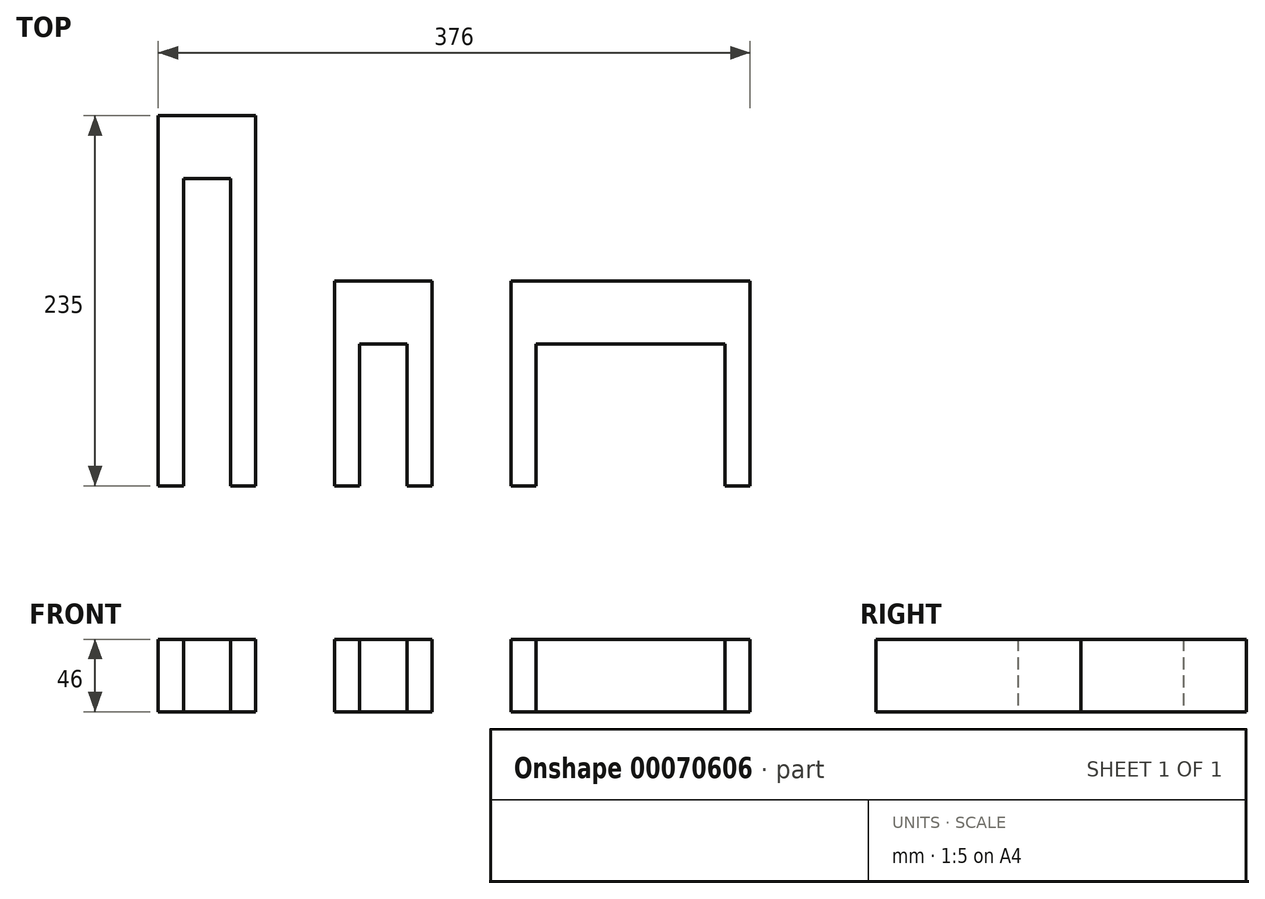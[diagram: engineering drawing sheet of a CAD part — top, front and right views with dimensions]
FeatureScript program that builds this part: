
annotation { "Feature Type Name" : "Feature", "Feature Type Description" : "" }
export const myFeature = defineFeature(function(context is Context, id is Id, definition is map)
    precondition{}
    {
        {
            var Q0;
            Q0=qCreatedBy(makeId("Top.planeOp"),FACE);
            var sketch = newSketch(context, id + "F0", { "sketchPlane" : qUnion([Q0])});
            skLineSegment(sketch, "E0.bottom", {"start": v(-62, 235) * mm, "end": v(0, 235) * mm});
            skLineSegment(sketch, "E0.top", {"start": v(-62, 0) * mm, "end": v(0, 0) * mm});
            skLineSegment(sketch, "E0.left", {"start": v(-62, 235) * mm, "end": v(-62, 0) * mm});
            skLineSegment(sketch, "E0.right", {"start": v(0, 235) * mm, "end": v(0, 0) * mm});
            skLineSegment(sketch, "E1.bottom", {"start": v(50, 130) * mm, "end": v(112, 130) * mm});
            skLineSegment(sketch, "E1.top", {"start": v(50, 0) * mm, "end": v(112, 0) * mm});
            skLineSegment(sketch, "E1.left", {"start": v(50, 130) * mm, "end": v(50, 0) * mm});
            skLineSegment(sketch, "E1.right", {"start": v(112, 130) * mm, "end": v(112, 0) * mm});
            skLineSegment(sketch, "E2.bottom", {"start": v(162, 0) * mm, "end": v(314, 0) * mm});
            skLineSegment(sketch, "E2.top", {"start": v(162, 130) * mm, "end": v(314, 130) * mm});
            skLineSegment(sketch, "E2.left", {"start": v(162, 0) * mm, "end": v(162, 130) * mm});
            skLineSegment(sketch, "E2.right", {"start": v(314, 0) * mm, "end": v(314, 130) * mm});
            skLineSegment(sketch, "E3.bottom", {"start": v(-46, 0) * mm, "end": v(-16, 0) * mm});
            skLineSegment(sketch, "E3.top", {"start": v(-46, 195) * mm, "end": v(-16, 195) * mm});
            skLineSegment(sketch, "E3.left", {"start": v(-46, 0) * mm, "end": v(-46, 195) * mm});
            skLineSegment(sketch, "E3.right", {"start": v(-16, 0) * mm, "end": v(-16, 195) * mm});
            skLineSegment(sketch, "E4.bottom", {"start": v(66, 0) * mm, "end": v(96, 0) * mm});
            skLineSegment(sketch, "E4.top", {"start": v(66, 90) * mm, "end": v(96, 90) * mm});
            skLineSegment(sketch, "E4.left", {"start": v(66, 0) * mm, "end": v(66, 90) * mm});
            skLineSegment(sketch, "E4.right", {"start": v(96, 0) * mm, "end": v(96, 90) * mm});
            skLineSegment(sketch, "E5.bottom", {"start": v(178, 0) * mm, "end": v(298, 0) * mm});
            skLineSegment(sketch, "E5.top", {"start": v(178, 90) * mm, "end": v(298, 90) * mm});
            skLineSegment(sketch, "E5.left", {"start": v(298, 0) * mm, "end": v(298, 90) * mm});
            skLineSegment(sketch, "E5.right", {"start": v(178, 0) * mm, "end": v(178, 90) * mm});
            skLineSegment(sketch, "E6", {"start": v(-31, 235) * mm, "end": v(-31, 0) * mm, "construction": true});
            skLineSegment(sketch, "E7", {"start": v(81, 130) * mm, "end": v(81, 0) * mm, "construction": true});
            skLineSegment(sketch, "E8", {"start": v(238, 130) * mm, "end": v(238, 0) * mm, "construction": true});
            skPoint(sketch, "E9", {"position": v(-31, 195) * mm});
            skPoint(sketch, "E10", {"position": v(81, 90) * mm});
            skPoint(sketch, "E11", {"position": v(238, 90) * mm});
            skLineSegment(sketch, "E12", {"start": v(0, 0) * mm, "end": v(50, 0) * mm, "construction": true});
            skLineSegment(sketch, "E13", {"start": v(112, 0) * mm, "end": v(162, 0) * mm, "construction": true});
            skSolve(sketch);
        }
        {
            var Q0;
            Q0=makeQuery(id+"F0.imprint","IMPRINT",FACE,{"disambiguationData":[TD([[makeQuery(id+"F0.imprint","IMPRINT",EDGE,{"derivedFrom":sQuery(id+"F0.wireOp",EDGE,"E0.bottom")}),-1.0]])]});
            var Q1;
            Q1=makeQuery(id+"F0.imprint","IMPRINT",FACE,{"disambiguationData":[TD([[makeQuery(id+"F0.imprint","IMPRINT",EDGE,{"derivedFrom":sQuery(id+"F0.wireOp",EDGE,"E3.bottom")}),1.0]])]});
            var Q2;
            Q2=makeQuery(id+"F0.imprint","IMPRINT",FACE,{"disambiguationData":[TD([[makeQuery(id+"F0.imprint","IMPRINT",EDGE,{"derivedFrom":sQuery(id+"F0.wireOp",EDGE,"E1.bottom")}),-1.0]])]});
            var Q3;
            Q3=makeQuery(id+"F0.imprint","IMPRINT",FACE,{"disambiguationData":[TD([[makeQuery(id+"F0.imprint","IMPRINT",EDGE,{"derivedFrom":sQuery(id+"F0.wireOp",EDGE,"E4.bottom")}),1.0]])]});
            var Q4;
            Q4=makeQuery(id+"F0.imprint","IMPRINT",FACE,{"disambiguationData":[TD([[makeQuery(id+"F0.imprint","IMPRINT",EDGE,{"derivedFrom":sQuery(id+"F0.wireOp",EDGE,"E2.top")}),-1.0]])]});
            var Q5;
            Q5=makeQuery(id+"F0.imprint","IMPRINT",FACE,{"disambiguationData":[TD([[makeQuery(id+"F0.imprint","IMPRINT",EDGE,{"derivedFrom":sQuery(id+"F0.wireOp",EDGE,"E5.bottom")}),1.0]])]});
            extrude(context, id + "F1", {"entities" : qUnion([Q0, Q1, Q2, Q3, Q4, Q5]), "depth" : 16 * mm, "hasSecondDirection" : true, "secondDirectionOppositeDirection" : true, "secondDirectionDepth" : 30 * mm});
        }
    });
